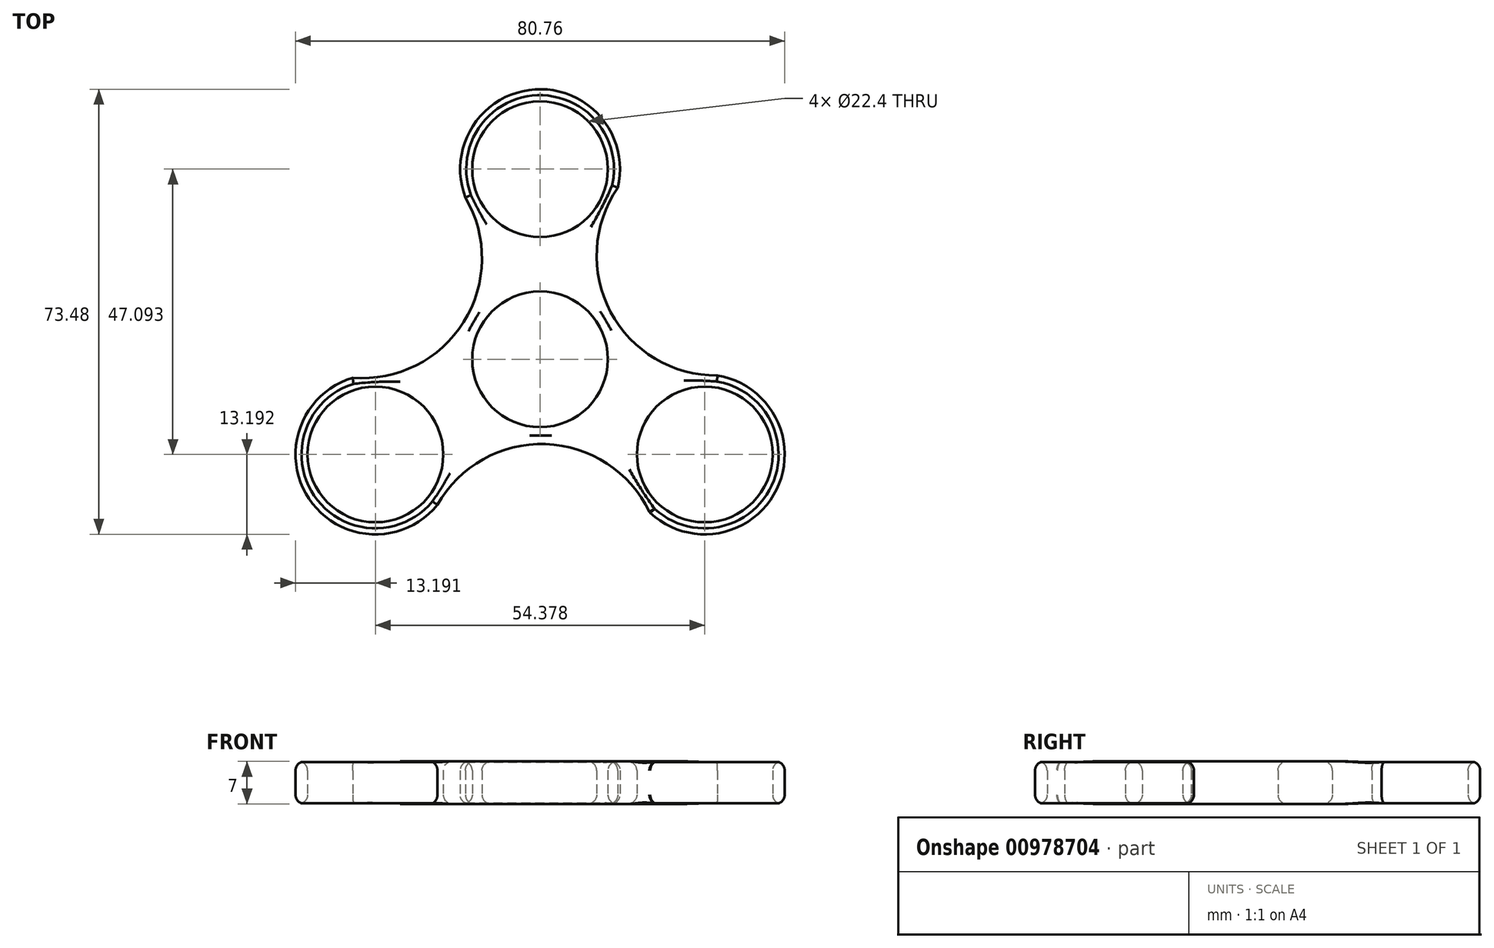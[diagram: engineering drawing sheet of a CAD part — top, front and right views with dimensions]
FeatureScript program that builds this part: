
annotation { "Feature Type Name" : "Feature", "Feature Type Description" : "" }
export const myFeature = defineFeature(function(context is Context, id is Id, definition is map)
    precondition{}
    {
        {
            var Q0;
            Q0=qCreatedBy(makeId("Top.planeOp"),FACE);
            var sketch = newSketch(context, id + "F0", { "sketchPlane" : qUnion([Q0])});
            skCircle(sketch, "E0", {"center": v(0, 0) * mm, "radius": 11.2 * mm});
            skCircle(sketch, "E1", {"center": v(0, 31.4) * mm, "radius": 11.2 * mm});
            skArc(sketch, "E2", {"start": v(10.28, 23.12) * mm, "mid": v(0.73, 44.57) * mm, "end": v(-11.14, 24.32) * mm});
            skPoint(sketch, "E3.center", {"position": v(2.89, -5) * mm});
            skArc(sketch, "E4.1.0", {"start": v(-25.17, -2.66) * mm, "mid": v(-38.97, -21.65) * mm, "end": v(-15.5, -21.8) * mm});
            skCircle(sketch, "E4.1.1", {"center": v(-27.19, -15.7) * mm, "radius": 11.2 * mm});
            skArc(sketch, "E4.2.0", {"start": v(14.89, -20.47) * mm, "mid": v(38.23, -22.92) * mm, "end": v(26.63, -2.51) * mm});
            skCircle(sketch, "E4.2.1", {"center": v(27.19, -15.7) * mm, "radius": 11.2 * mm});
            skArc(sketch, "E5", {"start": v(-30.93, -3.04) * mm, "mid": v(-12.6, 6.17) * mm, "end": v(-12.33, 26.7) * mm});
            skArc(sketch, "E6.1.0", {"start": v(18.1, -25.27) * mm, "mid": v(0.95, -14) * mm, "end": v(-16.95, -24.02) * mm});
            skArc(sketch, "E6.2.0", {"start": v(12.83, 28.3) * mm, "mid": v(11.65, 7.82) * mm, "end": v(29.28, -2.67) * mm});
            skSolve(sketch);
        }
        {
            var Q0;
            Q0=makeQuery(id+"F0.imprint","IMPRINT",FACE,{"disambiguationData":[TD([[makeQuery(id+"F0.imprint","IMPRINT",EDGE,{"derivedFrom":sQuery(id+"F0.wireOp",EDGE,"E0")}),-1.0]])]});
            extrude(context, id + "F1", {"entities" : qUnion([Q0]), "depth" : 7 * mm, "offsetDistance" : 25.4 * mm});
        }
        {
            var Q0;
            Q0=makeQuery(id+"F1.opExtrude","CAP_FACE",FACE,{"disambiguationData":[OSD([sQuery(id+"F0.wireOp",EDGE,"E0"),sQuery(id+"F0.wireOp",EDGE,"E1"),sQuery(id+"F0.wireOp",EDGE,"E2"),sQuery(id+"F0.wireOp",EDGE,"E4.1.0"),sQuery(id+"F0.wireOp",EDGE,"E4.1.1"),sQuery(id+"F0.wireOp",EDGE,"E4.2.0"),sQuery(id+"F0.wireOp",EDGE,"E4.2.1"),sQuery(id+"F0.wireOp",EDGE,"E5"),sQuery(id+"F0.wireOp",EDGE,"E6.1.0"),sQuery(id+"F0.wireOp",EDGE,"E6.2.0")])],"isStart":true});
            var Q1;
            Q1=makeQuery(id+"F1.opExtrude","CAP_FACE",FACE,{"disambiguationData":[OSD([sQuery(id+"F0.wireOp",EDGE,"E0"),sQuery(id+"F0.wireOp",EDGE,"E1"),sQuery(id+"F0.wireOp",EDGE,"E2"),sQuery(id+"F0.wireOp",EDGE,"E4.1.0"),sQuery(id+"F0.wireOp",EDGE,"E4.1.1"),sQuery(id+"F0.wireOp",EDGE,"E4.2.0"),sQuery(id+"F0.wireOp",EDGE,"E4.2.1"),sQuery(id+"F0.wireOp",EDGE,"E5"),sQuery(id+"F0.wireOp",EDGE,"E6.1.0"),sQuery(id+"F0.wireOp",EDGE,"E6.2.0")])],"isStart":false});
            fillet(context, id + "F2", {"entities" : qUnion([Q0, Q1]), "radius" : 1.5 * mm, "tangentPropagation" : true, "allowEdgeOverflow" : false});
        }
        {
            var Q0;
            Q0=makeQuery(id+"F1.opExtrude","SWEPT_EDGE",EDGE,{"disambiguationData":[OSD([sQuery(id+"F0.wireOp",EDGE,"E4.2.0"),sQuery(id+"F0.wireOp",EDGE,"E6.1.0")])]});
            fillet(context, id + "F3", {"entities" : qUnion([Q0]), "radius" : 0.58 * mm, "tangentPropagation" : true, "allowEdgeOverflow" : false});
        }
    });
